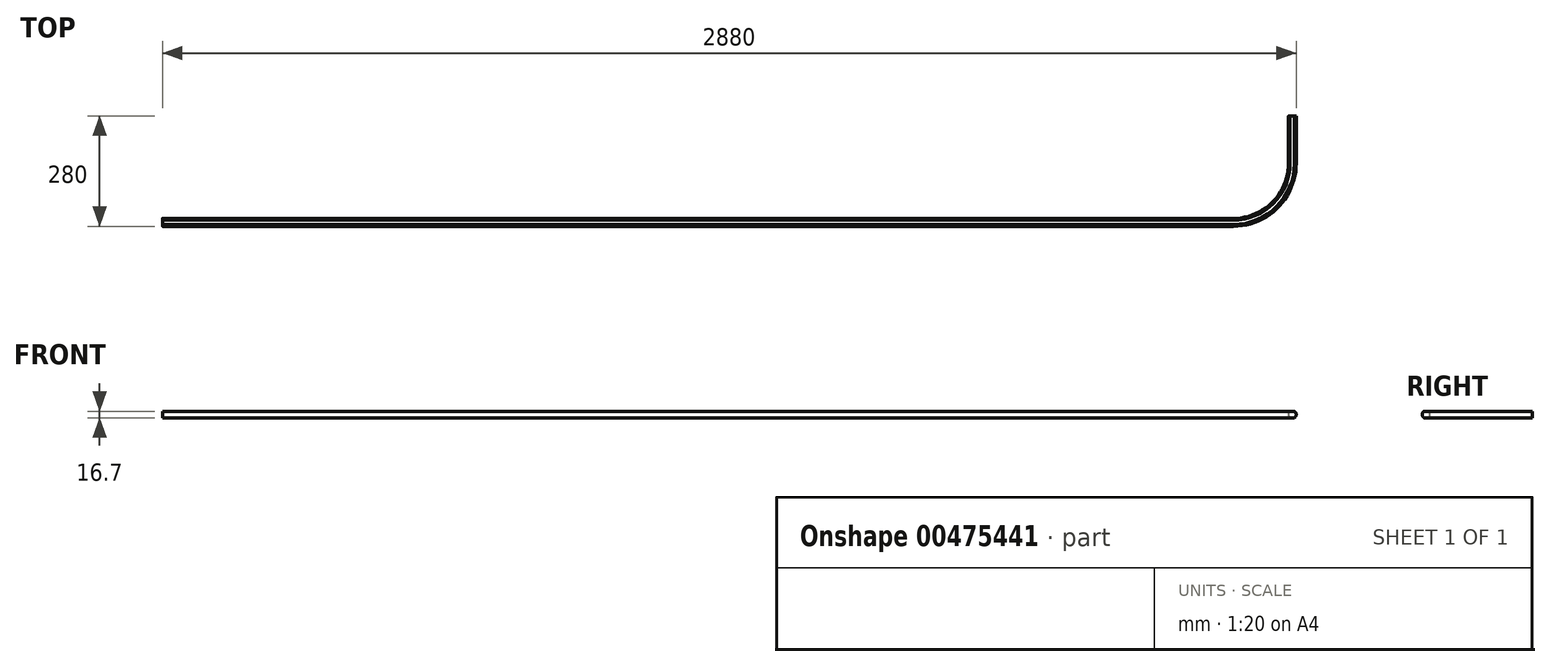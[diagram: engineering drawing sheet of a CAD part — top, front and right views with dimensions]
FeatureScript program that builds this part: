
annotation { "Feature Type Name" : "Feature", "Feature Type Description" : "" }
export const myFeature = defineFeature(function(context is Context, id is Id, definition is map)
    precondition{}
    {
        {
            var Q0;
            Q0=qCreatedBy(makeId("Top.planeOp"),FACE);
            var sketch = newSketch(context, id + "F0", { "sketchPlane" : qUnion([Q0])});
            skLineSegment(sketch, "E0", {"start": v(0, 0) * mm, "end": v(2720, 0) * mm});
            skLineSegment(sketch, "E1", {"start": v(2870, 150) * mm, "end": v(2870, 270) * mm});
            skPoint(sketch, "E2.visualSharp", {"position": v(2870, 0) * mm});
            skArc(sketch, "E2.filletArc", {"start": v(2720, 0) * mm, "mid": v(2826.07, 43.93) * mm, "end": v(2870, 150) * mm});
            skSolve(sketch);
        }
        {
            var Q0;
            Q0=qCreatedBy(makeId("Right.planeOp"),FACE);
            var sketch = newSketch(context, id + "F1", { "sketchPlane" : qUnion([Q0])});
            skCircle(sketch, "E3", {"center": v(0, 0) * mm, "radius": 10 * mm});
            skLineSegment(sketch, "E4", {"start": v(5.5, 8.35) * mm, "end": v(-5.5, 8.35) * mm});
            skLineSegment(sketch, "E5", {"start": v(5.5, -8.35) * mm, "end": v(-5.5, -8.35) * mm});
            skSolve(sketch);
        }
        {
            var Q0;
            Q0=makeQuery(id+"F1.imprint","IMPRINT",FACE,{"disambiguationData":[TD([[makeQuery(id+"F1.imprint","IMPRINT",EDGE,{"derivedFrom":sQuery(id+"F1.wireOp",EDGE,"E3")}),1.0]])]});
            var Q1;
            Q1=sQuery(id+"F0.wireOp",EDGE,"E0");
            var Q2;
            Q2=sQuery(id+"F0.wireOp",EDGE,"E2.filletArc");
            var Q3;
            Q3=sQuery(id+"F0.wireOp",EDGE,"E1");
            sweep(context, id + "F2", {"profiles" : qUnion([Q0]), "path" : qUnion([Q1, Q2, Q3])});
        }
    });
